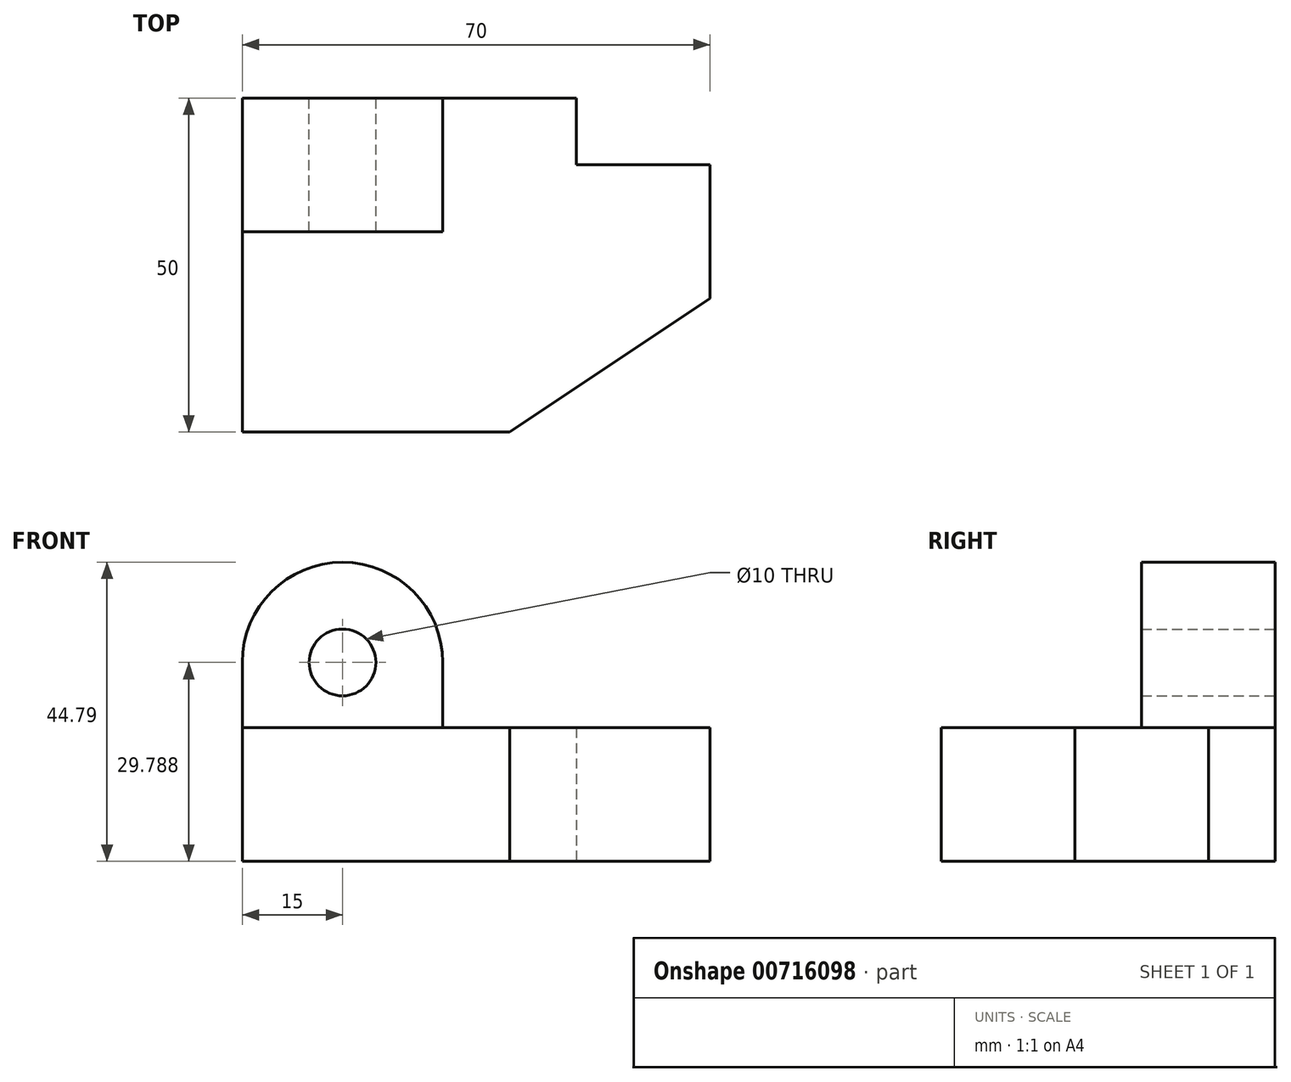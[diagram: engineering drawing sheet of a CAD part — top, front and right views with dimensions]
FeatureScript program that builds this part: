
annotation { "Feature Type Name" : "Feature", "Feature Type Description" : "" }
export const myFeature = defineFeature(function(context is Context, id is Id, definition is map)
    precondition{}
    {
        {
            var Q0;
            Q0=qCreatedBy(makeId("Top.planeOp"),FACE);
            var sketch = newSketch(context, id + "F0", { "sketchPlane" : qUnion([Q0])});
            skLineSegment(sketch, "E0", {"start": v(0, 0) * mm, "end": v(40, 0) * mm});
            skLineSegment(sketch, "E1", {"start": v(40, 0) * mm, "end": v(70, 20) * mm});
            skLineSegment(sketch, "E2", {"start": v(70, 20) * mm, "end": v(70, 40) * mm});
            skLineSegment(sketch, "E3", {"start": v(70, 40) * mm, "end": v(50, 40) * mm});
            skLineSegment(sketch, "E4", {"start": v(50, 40) * mm, "end": v(50, 50) * mm});
            skLineSegment(sketch, "E5", {"start": v(50, 50) * mm, "end": v(0, 50) * mm});
            skLineSegment(sketch, "E6", {"start": v(0, 50) * mm, "end": v(0, 0) * mm});
            skSolve(sketch);
        }
        {
            var Q0;
            Q0 = qSketchRegion(id + "F0", true);
            var Q1;
            Q1=makeQuery(id+"F0.imprint","IMPRINT",FACE,{"disambiguationData":[TD([[makeQuery(id+"F0.imprint","IMPRINT",EDGE,{"derivedFrom":sQuery(id+"F0.wireOp",EDGE,"E0")}),1.0]])]});
            extrude(context, id + "F1", {"entities" : qUnion([Q0, Q1]), "depth" : 20 * mm, "offsetDistance" : 25 * mm});
        }
        {
            var Q0;
            Q0=makeQuery(id+"F1.opExtrude","SWEPT_FACE",FACE,{"disambiguationData":[OSD([sQuery(id+"F0.wireOp",EDGE,"E5")])]});
            var sketch = newSketch(context, id + "F2", { "sketchPlane" : qUnion([Q0])});
            skLineSegment(sketch, "E7", {"start": v(0, 20) * mm, "end": v(0, 29.79) * mm});
            skLineSegment(sketch, "E8", {"start": v(0, 29.79) * mm, "end": v(-30, 29.79) * mm});
            skLineSegment(sketch, "E9", {"start": v(-30, 29.79) * mm, "end": v(-30, 20) * mm});
            skLineSegment(sketch, "E10", {"start": v(-30, 20) * mm, "end": v(0, 20) * mm});
            skCircle(sketch, "E11", {"center": v(-15, 29.79) * mm, "radius": 15 * mm});
            skSolve(sketch);
        }
        {
            var Q0;
            {var subQ0=sQuery(id+"F2.wireOp",EDGE,"E7");Q0=makeQuery(id+"F2.imprint","IMPRINT",FACE,{"disambiguationData":[TD([[makeQuery(id+"F2.imprint","IMPRINT",EDGE,{"derivedFrom":subQ0}),1.0]])]});}
            var Q1;
            {var subQ0=sQuery(id+"F2.wireOp",EDGE,"E9");Q1=makeQuery(id+"F2.imprint","IMPRINT",FACE,{"disambiguationData":[TD([[makeQuery(id+"F2.imprint","IMPRINT",EDGE,{"derivedFrom":subQ0}),1.0]])]});}
            var Q2;
            {var subQ0=sQuery(id+"F2.wireOp",EDGE,"E11");var subQ1=sQuery(id+"F2.wireOp",EDGE,"E10");var subQ2=makeQuery(id+"F2.imprint","INTERSECT",VERTEX,{"disambiguationData":[OD(0.0)],"derivedFrom":[subQ1,subQ0]});Q2=makeQuery(id+"F2.imprint","IMPRINT",FACE,{"disambiguationData":[TD([[makeQuery(id+"F2.imprint","IMPRINT",EDGE,{"disambiguationData":[TD([[subQ2,-1.0]])],"derivedFrom":subQ1}),-1.0]])]});}
            var Q3;
            {var subQ0=sQuery(id+"F2.wireOp",EDGE,"E8");Q3=makeQuery(id+"F2.imprint","IMPRINT",FACE,{"disambiguationData":[TD([[makeQuery(id+"F2.imprint","IMPRINT",EDGE,{"derivedFrom":subQ0}),-1.0]])]});}
            var Q4;
            {var subQ0=sQuery(id+"F2.wireOp",EDGE,"E8");Q4=makeQuery(id+"F2.imprint","IMPRINT",FACE,{"disambiguationData":[TD([[makeQuery(id+"F2.imprint","IMPRINT",EDGE,{"derivedFrom":subQ0}),1.0]])]});}
            extrude(context, id + "F3", {"entities" : qUnion([Q0, Q1, Q2, Q3, Q4]), "operationType" : NewBodyOperationType.ADD, "oppositeDirection" : true, "depth" : 20 * mm, "offsetDistance" : 25 * mm});
        }
        {
            var Q0;
            Q0=makeQuery(id+"F3.boolean.opBoolean","MERGE",FACE,{"derivedFrom":[makeQuery(id+"F1.opExtrude","SWEPT_FACE",FACE,{"disambiguationData":[OSD([sQuery(id+"F0.wireOp",EDGE,"E5")])]}),makeQuery(id+"F3.opExtrude","CAP_FACE",FACE,{"disambiguationData":[OSD([sQuery(id+"F2.wireOp",EDGE,"E7"),sQuery(id+"F2.wireOp",EDGE,"E9"),sQuery(id+"F2.wireOp",EDGE,"E10"),sQuery(id+"F2.wireOp",EDGE,"E11")])],"isStart":true})]});
            var sketch = newSketch(context, id + "F4", { "sketchPlane" : qUnion([Q0])});
            skCircle(sketch, "E12", {"center": v(-15, 29.79) * mm, "radius": 5 * mm});
            skSolve(sketch);
        }
        {
            var Q0;
            Q0 = qSketchRegion(id + "F4", true);
            extrude(context, id + "F5", {"entities" : qUnion([Q0]), "operationType" : NewBodyOperationType.REMOVE, "endBound" : BoundingType.UP_TO_NEXT, "oppositeDirection" : true, "depth" : 25 * mm, "offsetDistance" : 25 * mm});
        }
    });
